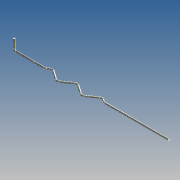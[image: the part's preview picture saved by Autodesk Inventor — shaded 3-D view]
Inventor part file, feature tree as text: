
AUTODESK INVENTOR PART (.ipt)
format: ipt  version: 2016 (Build 200138000, 138)  size: 124,416 bytes
history: native  units: mm
features: sketch x3, plane x1, sweep x1, direct_edit x1, move_body x1
ambient origin geometry x8: Origin, YZ Plane, XZ Plane, XY Plane, X Axis, Y Axis, Z Axis, Center Point
bodies: Body1 (feature_tree)
feature tree (7):
  sketch  "Sketch1"  dims[d0=160.0mm d1=50.0mm]
  sketch  "3D Sketch1"
  plane  "Work Plane1"
  sweep  "Sweep2"
  direct_edit  "Direct Edit1"
  sketch  "Sketch2"  dims[d2=20.0mm d3=20.0mm d4=20.0mm d5=20.0mm d6=20.0mm d7=14.0mm d8=5.0mm d9=15.714286mm d11=2.5mm d14=5.0mm d15=17.0mm d16=90.0deg d17=3.0mm d18=0.0mm d19=0.0mm d23=0.0mm d24=0.0mm d25=-25.0mm]
  move_body  "Move2"
